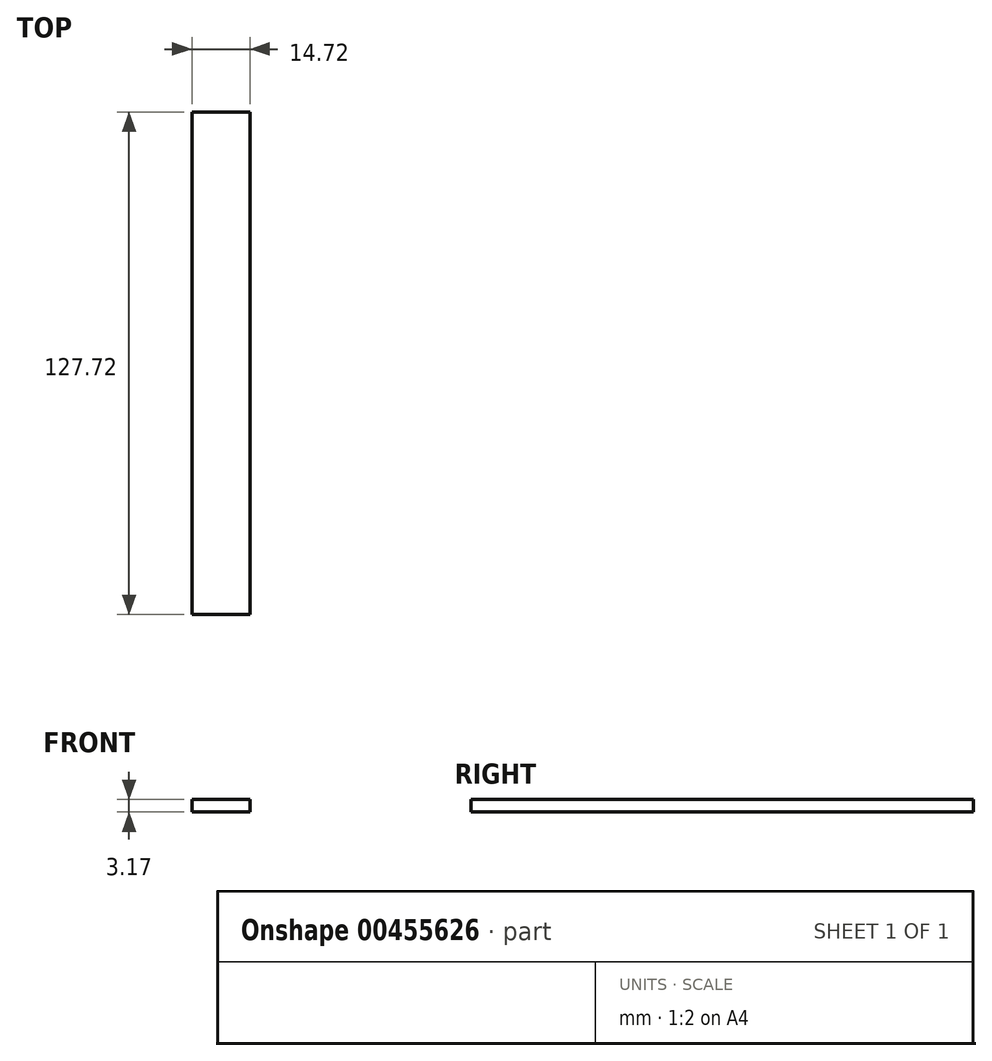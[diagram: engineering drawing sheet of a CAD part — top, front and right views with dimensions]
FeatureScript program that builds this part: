
annotation { "Feature Type Name" : "Feature", "Feature Type Description" : "" }
export const myFeature = defineFeature(function(context is Context, id is Id, definition is map)
    precondition{}
    {
        {
            var Q0;
            Q0=qCreatedBy(makeId("Top.planeOp"),FACE);
            var sketch = newSketch(context, id + "F0", { "sketchPlane" : qUnion([Q0])});
            skLineSegment(sketch, "E0.bottom", {"start": v(7.36, 63.86) * mm, "end": v(-7.36, 63.86) * mm});
            skLineSegment(sketch, "E0.top", {"start": v(7.36, -63.86) * mm, "end": v(-7.36, -63.86) * mm});
            skLineSegment(sketch, "E0.left", {"start": v(7.36, 63.86) * mm, "end": v(7.36, -63.86) * mm});
            skLineSegment(sketch, "E0.right", {"start": v(-7.36, 63.86) * mm, "end": v(-7.36, -63.86) * mm});
            skPoint(sketch, "E0.middle", {"position": v(0, 0) * mm});
            skSolve(sketch);
        }
        {
            var Q0;
            Q0=makeQuery(id+"F0.imprint","IMPRINT",FACE,{"disambiguationData":[TD([[makeQuery(id+"F0.imprint","IMPRINT",EDGE,{"derivedFrom":sQuery(id+"F0.wireOp",EDGE,"E0.bottom")}),1.0]])]});
            extrude(context, id + "F1", {"entities" : qUnion([Q0]), "depth" : 3.17 * mm});
        }
    });
